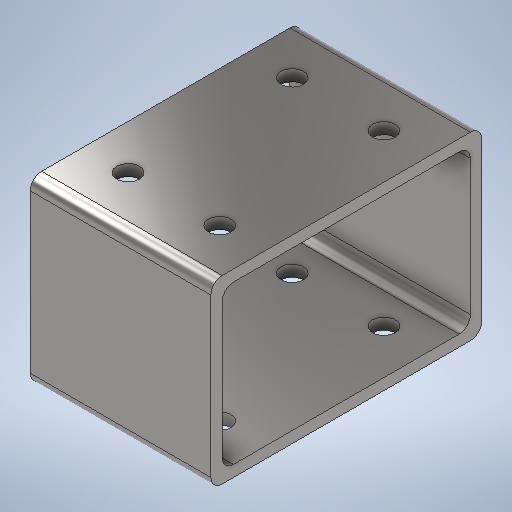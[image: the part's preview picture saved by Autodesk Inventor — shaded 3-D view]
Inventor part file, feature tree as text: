
AUTODESK INVENTOR PART (.ipt)
format: ipt  version: 2025.2 (Build 292293000, 293)  size: 294,912 bytes
history: native  units: in
note: dims shown in document units (in); Inventor stores cm internally (conversion verified against a paired STEP export)
features: extrude x5, sketch x2, shell x1, fillet x1
ambient origin geometry x8: Origin, YZ Plane, XZ Plane, XY Plane, X Axis, Y Axis, Z Axis, Center Point
bodies: Solid1 (feature_tree)
feature tree (9):
  extrude  "Extrusion1"  Depth=2.0in
  shell  "Shell1"  Thickness=2.0in
  fillet  "Fillet1"  Radius=0.125in
  extrude  "Extrusion2"  Depth=2.0in
  extrude  "Extrusion4"  Depth=2.0in
  extrude  "Extrusion3"  Depth=3.0in
  extrude  "Extrusion5"  Depth=2.0in
  sketch  "Sketch4"  dims[d0=3.0in d1=2.0in d2=2.0in d3=0.0in d4=0.125in]
  sketch  "Sketch5"  dims[d5=0.125in d6=0.25in d7=2.0in d8=3.0in d10=0.4921in d11=0.5906in d12=0.0in d13=0.0in d14=0.125in d15=3.0in d16=2.0in d17=0.25in d21=1.0in d22=0.0in d23=0.25in d24=1.0in d25=0.0in d26=0.0in d27=0.0in d28=0.9843in]
